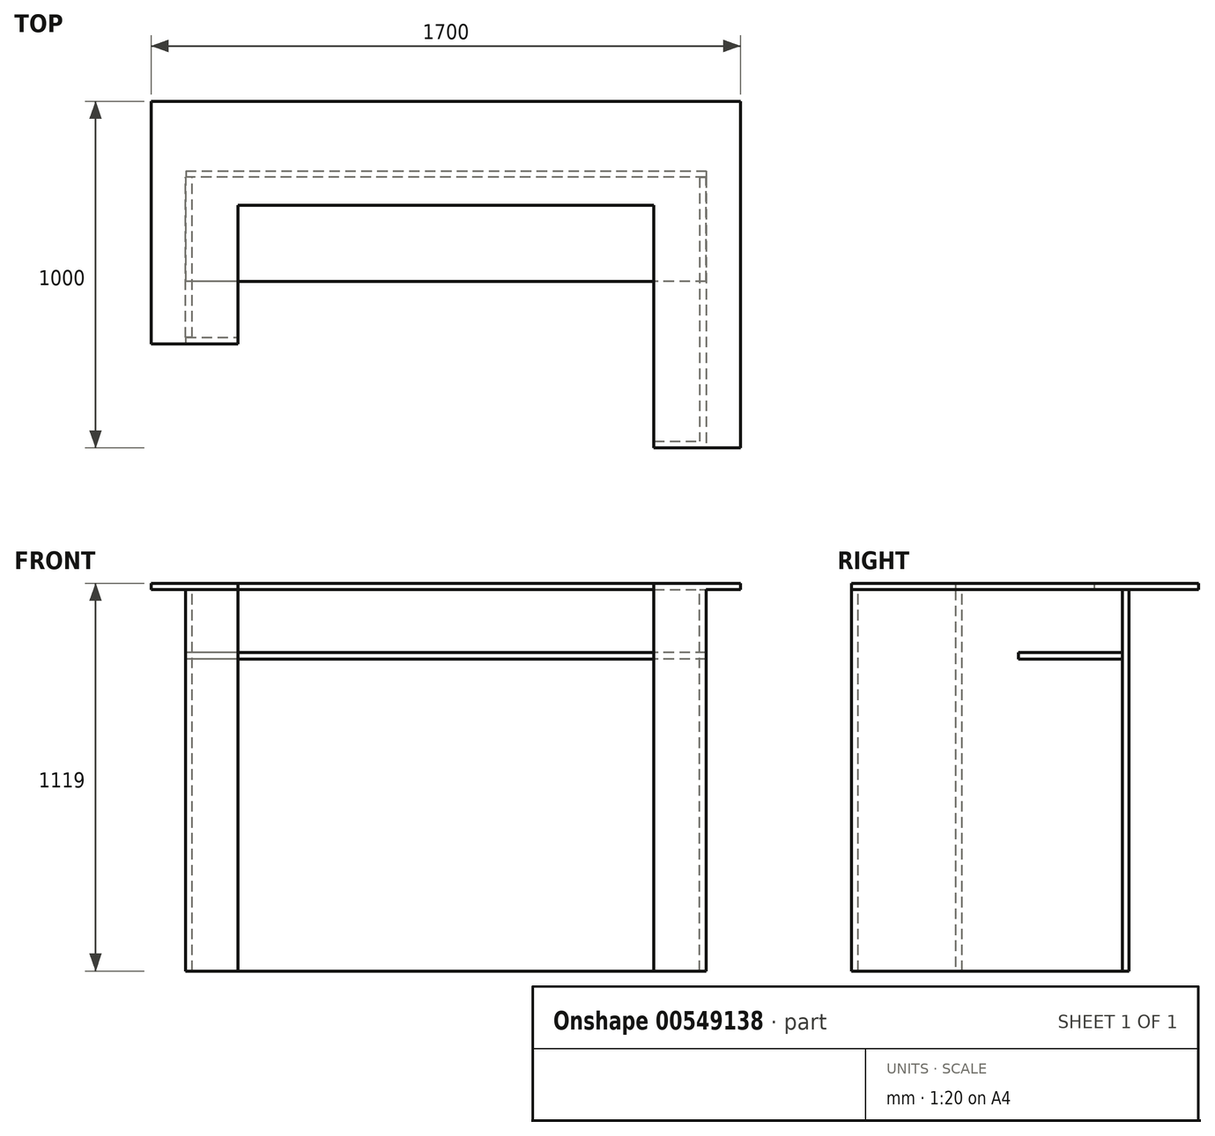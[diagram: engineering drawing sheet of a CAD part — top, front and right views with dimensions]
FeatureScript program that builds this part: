
annotation { "Feature Type Name" : "Feature", "Feature Type Description" : "" }
export const myFeature = defineFeature(function(context is Context, id is Id, definition is map)
    precondition{}
    {
        {
            var Q0;
            Q0=qCreatedBy(makeId("Top.planeOp"),FACE);
            var sketch = newSketch(context, id + "F0", { "sketchPlane" : qUnion([Q0])});
            skLineSegment(sketch, "E0.bottom", {"start": v(-833.46, -580.9) * mm, "end": v(866.54, -580.9) * mm});
            skLineSegment(sketch, "E0.top", {"start": v(-833.46, -280.9) * mm, "end": v(866.54, -280.9) * mm});
            skLineSegment(sketch, "E0.left", {"start": v(-833.46, -580.9) * mm, "end": v(-833.46, -280.9) * mm});
            skLineSegment(sketch, "E0.right", {"start": v(866.54, -580.9) * mm, "end": v(866.54, -280.9) * mm});
            skLineSegment(sketch, "E1.bottom", {"start": v(866.54, -580.9) * mm, "end": v(616.54, -580.9) * mm});
            skLineSegment(sketch, "E2.bottom", {"start": v(-833.46, -580.9) * mm, "end": v(-583.46, -580.9) * mm});
            skLineSegment(sketch, "E3.top", {"start": v(-833.46, -980.9) * mm, "end": v(-583.46, -980.9) * mm});
            skLineSegment(sketch, "E3.left", {"start": v(-833.46, -580.9) * mm, "end": v(-833.46, -980.9) * mm});
            skLineSegment(sketch, "E3.right", {"start": v(-583.46, -580.9) * mm, "end": v(-583.46, -980.9) * mm});
            skLineSegment(sketch, "E4.bottom", {"start": v(616.54, -580.9) * mm, "end": v(866.54, -580.9) * mm});
            skLineSegment(sketch, "E4.top", {"start": v(616.54, -1280.9) * mm, "end": v(866.54, -1280.9) * mm});
            skLineSegment(sketch, "E4.left", {"start": v(616.54, -580.9) * mm, "end": v(616.54, -1280.9) * mm});
            skLineSegment(sketch, "E4.right", {"start": v(866.54, -580.9) * mm, "end": v(866.54, -1280.9) * mm});
            skSolve(sketch);
        }
        {
            var Q0;
            Q0 = qSketchRegion(id + "F0", true);
            extrude(context, id + "F1", {"entities" : qUnion([Q0]), "depth" : 19 * mm, "offsetDistance" : 25 * mm});
        }
        {
            var Q0;
            Q0=makeQuery(id+"F1.opExtrude","SWEPT_FACE",FACE,{"disambiguationData":[OSD([sQuery(id+"F0.wireOp",EDGE,"E4.top")])]});
            var sketch = newSketch(context, id + "F2", { "sketchPlane" : qUnion([Q0])});
            skLineSegment(sketch, "E5", {"start": v(616.54, -1100) * mm, "end": v(766.54, -1100) * mm});
            skLineSegment(sketch, "E6", {"start": v(616.54, -1100) * mm, "end": v(616.54, 0) * mm});
            skLineSegment(sketch, "E7", {"start": v(766.54, -1100) * mm, "end": v(766.54, 0) * mm});
            skSolve(sketch);
        }
        {
            var Q0;
            Q0=makeQuery(id+"F2.imprint","IMPRINT",FACE,{"disambiguationData":[TD([[makeQuery(id+"F2.imprint","IMPRINT",EDGE,{"derivedFrom":sQuery(id+"F2.wireOp",EDGE,"E5")}),1.0]])]});
            extrude(context, id + "F3", {"entities" : qUnion([Q0]), "oppositeDirection" : true, "depth" : 19 * mm, "offsetDistance" : 25 * mm});
        }
        {
            var Q0;
            Q0=makeQuery(id+"F1.opExtrude","SWEPT_FACE",FACE,{"disambiguationData":[OSD([sQuery(id+"F0.wireOp",EDGE,"E3.top")])]});
            var sketch = newSketch(context, id + "F4", { "sketchPlane" : qUnion([Q0])});
            skLineSegment(sketch, "E8", {"start": v(-583.46, 0) * mm, "end": v(-583.46, -1100) * mm});
            skLineSegment(sketch, "E9", {"start": v(-733.46, -1100) * mm, "end": v(-583.46, -1100) * mm});
            skLineSegment(sketch, "E10", {"start": v(-733.46, -1100) * mm, "end": v(-733.46, 0) * mm});
            skPoint(sketch, "E10.endSnap0", {"position": v(-708.46, 0) * mm});
            skSolve(sketch);
        }
        {
            var Q0;
            Q0=makeQuery(id+"F4.imprint","IMPRINT",FACE,{"disambiguationData":[TD([[makeQuery(id+"F4.imprint","IMPRINT",EDGE,{"derivedFrom":sQuery(id+"F4.wireOp",EDGE,"E8")}),-1.0]])]});
            extrude(context, id + "F5", {"entities" : qUnion([Q0]), "oppositeDirection" : true, "depth" : 19 * mm, "offsetDistance" : 25 * mm});
        }
        {
            var Q0;
            Q0=makeQuery(id+"F3.opExtrude","SWEPT_FACE",FACE,{"disambiguationData":[OSD([sQuery(id+"F2.wireOp",EDGE,"E7")])]});
            var sketch = newSketch(context, id + "F6", { "sketchPlane" : qUnion([Q0])});
            skLineSegment(sketch, "E11", {"start": v(-1261.9, -1100) * mm, "end": v(-499.9, -1100) * mm});
            skLineSegment(sketch, "E12", {"start": v(-499.9, -1100) * mm, "end": v(-499.9, 0) * mm});
            skLineSegment(sketch, "E13", {"start": v(-499.9, 0) * mm, "end": v(-1261.9, 0) * mm});
            skSolve(sketch);
        }
        {
            var Q0;
            Q0=makeQuery(id+"F6.imprint","IMPRINT",FACE,{"disambiguationData":[TD([[makeQuery(id+"F6.imprint","IMPRINT",EDGE,{"derivedFrom":sQuery(id+"F6.wireOp",EDGE,"E11")}),1.0]])]});
            extrude(context, id + "F7", {"entities" : qUnion([Q0]), "operationType" : NewBodyOperationType.ADD, "oppositeDirection" : true, "depth" : 19 * mm, "offsetDistance" : 25 * mm});
        }
        {
            var Q0;
            Q0=makeQuery(id+"F5.opExtrude","SWEPT_FACE",FACE,{"disambiguationData":[OSD([sQuery(id+"F4.wireOp",EDGE,"E10")])]});
            var sketch = newSketch(context, id + "F8", { "sketchPlane" : qUnion([Q0])});
            skPoint(sketch, "E14.start.orphan", {"position": v(461.9, 0) * mm});
            skLineSegment(sketch, "E15", {"start": v(961.9, -1100) * mm, "end": v(499.9, -1100) * mm});
            skLineSegment(sketch, "E16", {"start": v(499.9, -1100) * mm, "end": v(499.9, 0) * mm});
            skLineSegment(sketch, "E17", {"start": v(499.9, 0) * mm, "end": v(961.9, 0) * mm});
            skSolve(sketch);
        }
        {
            var Q0;
            Q0=makeQuery(id+"F8.imprint","IMPRINT",FACE,{"disambiguationData":[TD([[makeQuery(id+"F8.imprint","IMPRINT",EDGE,{"derivedFrom":sQuery(id+"F8.wireOp",EDGE,"E15")}),-1.0]])]});
            extrude(context, id + "F9", {"entities" : qUnion([Q0]), "oppositeDirection" : true, "depth" : 19 * mm, "offsetDistance" : 25 * mm});
        }
        {
            var Q0;
            Q0=makeQuery(id+"F7.opExtrude","SWEPT_FACE",FACE,{"disambiguationData":[OSD([sQuery(id+"F6.wireOp",EDGE,"E12")])]});
            var sketch = newSketch(context, id + "F10", { "sketchPlane" : qUnion([Q0])});
            skLineSegment(sketch, "E18", {"start": v(-766.54, -1100) * mm, "end": v(733.28, -1100) * mm});
            skLineSegment(sketch, "E19", {"start": v(733.28, -1100) * mm, "end": v(733.28, 0) * mm});
            skLineSegment(sketch, "E20", {"start": v(733.28, 0) * mm, "end": v(-766.54, 0) * mm});
            skLineSegment(sketch, "E21", {"start": v(-766.54, 0) * mm, "end": v(-766.54, -1100) * mm});
            skSolve(sketch);
        }
        {
            var Q0;
            Q0 = qSketchRegion(id + "F10", true);
            extrude(context, id + "F11", {"entities" : qUnion([Q0]), "depth" : 19 * mm, "offsetDistance" : 25 * mm});
        }
        {
            var Q0;
            Q0=makeQuery(id+"F11.opExtrude","CAP_FACE",FACE,{"disambiguationData":[OSD([sQuery(id+"F10.wireOp",EDGE,"E18"),sQuery(id+"F10.wireOp",EDGE,"E19"),sQuery(id+"F10.wireOp",EDGE,"E20"),sQuery(id+"F10.wireOp",EDGE,"E21")])],"isStart":true});
            var sketch = newSketch(context, id + "F12", { "sketchPlane" : qUnion([Q0])});
            skLineSegment(sketch, "E22", {"start": v(0, -1438.07) * mm, "end": v(518.96, -1438.07) * mm});
            skLineSegment(sketch, "E23.bottom", {"start": v(766.54, -200) * mm, "end": v(-733.28, -200) * mm});
            skLineSegment(sketch, "E23.top", {"start": v(766.54, -181) * mm, "end": v(-733.28, -181) * mm});
            skLineSegment(sketch, "E23.left", {"start": v(766.54, -200) * mm, "end": v(766.54, -181) * mm});
            skLineSegment(sketch, "E23.right", {"start": v(-733.28, -200) * mm, "end": v(-733.28, -181) * mm});
            skSolve(sketch);
        }
        {
            var Q0;
            Q0 = qSketchRegion(id + "F12", true);
            extrude(context, id + "F13", {"entities" : qUnion([Q0]), "depth" : 300 * mm, "offsetDistance" : 25 * mm});
        }
    });
